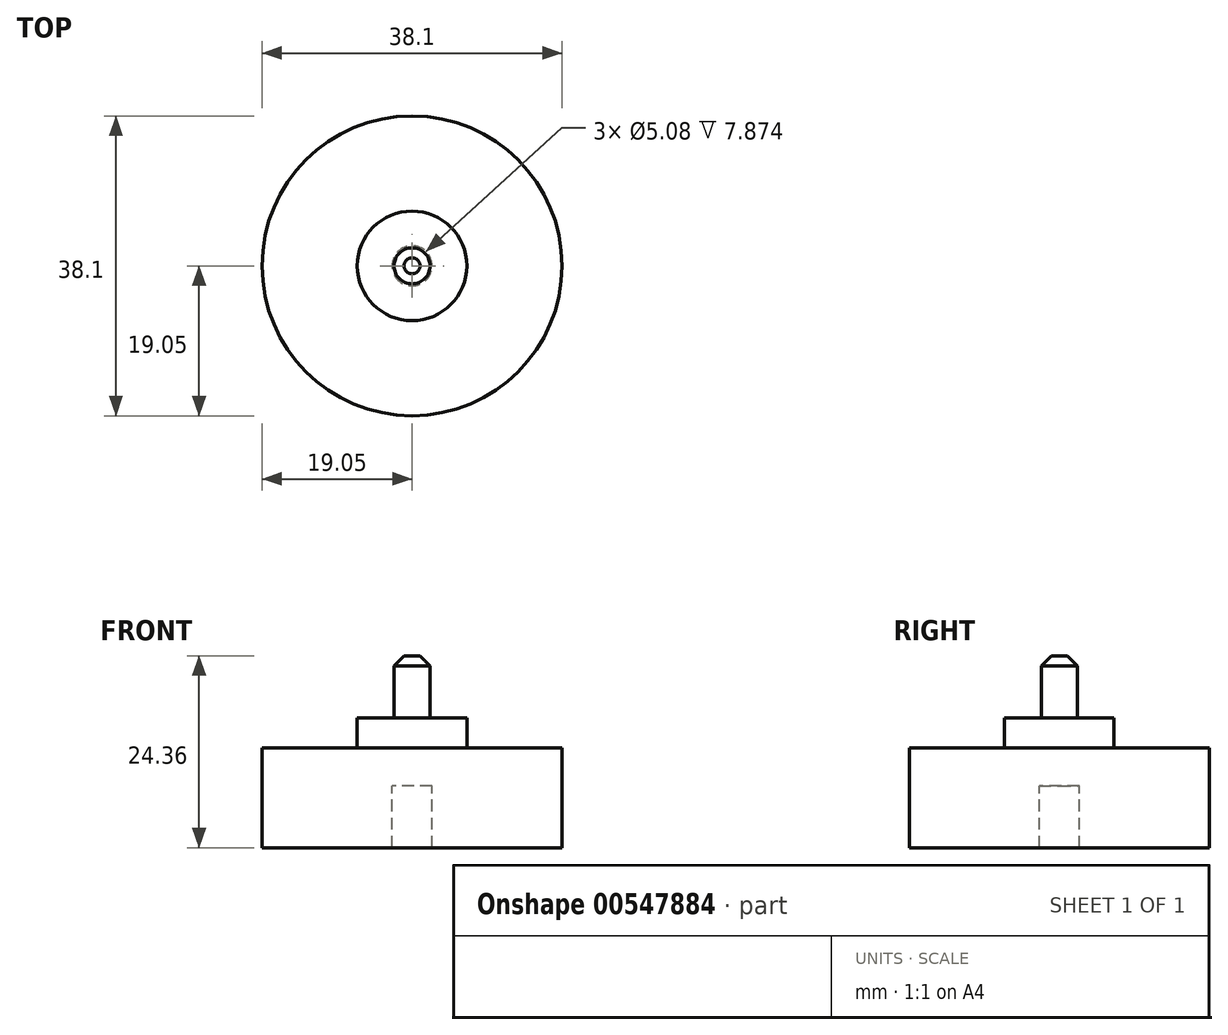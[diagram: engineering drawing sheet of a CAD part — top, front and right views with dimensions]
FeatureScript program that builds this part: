
annotation { "Feature Type Name" : "Feature", "Feature Type Description" : "" }
export const myFeature = defineFeature(function(context is Context, id is Id, definition is map)
    precondition{}
    {
        {
            var Q0;
            Q0=qCreatedBy(makeId("Front.planeOp"),FACE);
            var sketch = newSketch(context, id + "F0", { "sketchPlane" : qUnion([Q0])});
            skLineSegment(sketch, "E0", {"start": v(19.05, 12.7) * mm, "end": v(19.05, 0) * mm});
            skLineSegment(sketch, "E1", {"start": v(6.96, 16.51) * mm, "end": v(6.96, 12.7) * mm});
            skLineSegment(sketch, "E2", {"start": v(19.05, 12.7) * mm, "end": v(6.96, 12.7) * mm});
            skLineSegment(sketch, "E3", {"start": v(2.54, 0) * mm, "end": v(2.54, 7.87) * mm});
            skLineSegment(sketch, "E4", {"start": v(2.54, 7.87) * mm, "end": v(0, 7.87) * mm});
            skLineSegment(sketch, "E5", {"start": v(0, 24.36) * mm, "end": v(0, 7.87) * mm});
            skLineSegment(sketch, "E6", {"start": v(19.05, 0) * mm, "end": v(2.54, 0) * mm});
            skLineSegment(sketch, "E7", {"start": v(0, 24.36) * mm, "end": v(2.29, 24.36) * mm});
            skLineSegment(sketch, "E8", {"start": v(6.96, 16.51) * mm, "end": v(2.29, 16.51) * mm});
            skLineSegment(sketch, "E9", {"start": v(2.29, 24.36) * mm, "end": v(2.29, 16.51) * mm});
            skSolve(sketch);
        }
        {
            var Q0;
            Q0 = qSketchRegion(id + "F0", true);
            var Q1;
            Q1=sQuery(id+"F0.wireOp",EDGE,"E5");
            revolve(context, id + "F1", {"entities" : qUnion([Q0]), "axis" : qUnion([Q1]), "revolveType" : RevolveType.FULL});
        }
        {
            var Q0;
            Q0=makeQuery(id+"F1.opRevolve","SWEPT_EDGE",EDGE,{"disambiguationData":[OSD([sQuery(id+"F0.wireOp",EDGE,"E7"),sQuery(id+"F0.wireOp",EDGE,"E9")])]});
            chamfer(context, id + "F2", {"entities" : qUnion([Q0]), "width" : 1.27 * mm, "tangentPropagation" : true});
        }
    });
